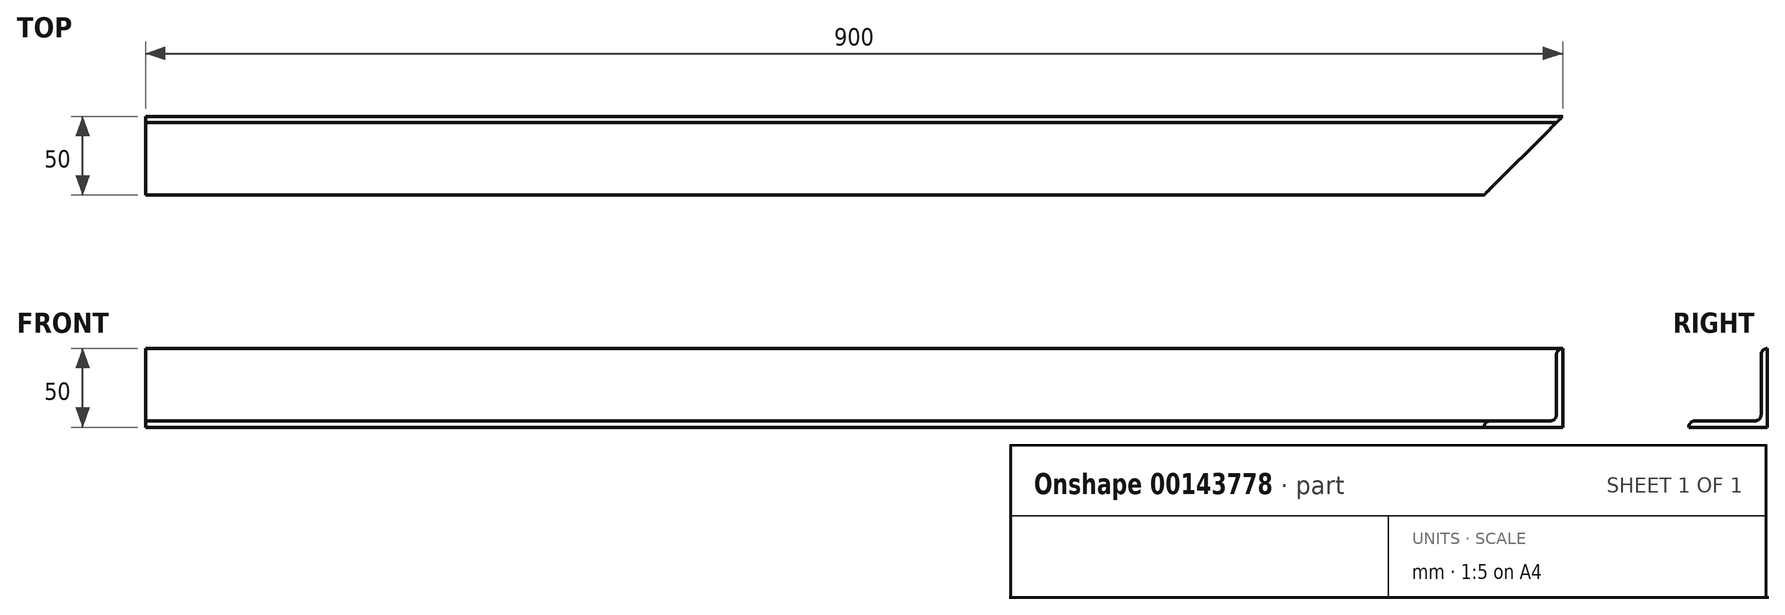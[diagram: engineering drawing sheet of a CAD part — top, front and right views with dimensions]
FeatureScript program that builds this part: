
annotation { "Feature Type Name" : "Feature", "Feature Type Description" : "" }
export const myFeature = defineFeature(function(context is Context, id is Id, definition is map)
    precondition{}
    {
        {
            var Q0;
            Q0=qCreatedBy(makeId("Right.planeOp"),FACE);
            var sketch = newSketch(context, id + "F0", { "sketchPlane" : qUnion([Q0])});
            skLineSegment(sketch, "E0", {"start": v(0, 50) * mm, "end": v(0, 0) * mm});
            skLineSegment(sketch, "E1", {"start": v(0, 0) * mm, "end": v(-50, 0) * mm});
            skLineSegment(sketch, "E2", {"start": v(0, 50) * mm, "end": v(0, 50) * mm});
            skLineSegment(sketch, "E3", {"start": v(-4, 46) * mm, "end": v(-4, 8) * mm});
            skLineSegment(sketch, "E4", {"start": v(-8, 4) * mm, "end": v(-46, 4) * mm});
            skLineSegment(sketch, "E5", {"start": v(-50, 0) * mm, "end": v(-50, 0) * mm});
            skPoint(sketch, "E6.visualSharp", {"position": v(-4, 50) * mm});
            skArc(sketch, "E6.filletArc", {"start": v(0, 50) * mm, "mid": v(-2.83, 48.83) * mm, "end": v(-4, 46) * mm});
            skPoint(sketch, "E7.visualSharp", {"position": v(-50, 4) * mm});
            skArc(sketch, "E7.filletArc", {"start": v(-46, 4) * mm, "mid": v(-48.83, 2.83) * mm, "end": v(-50, 0) * mm});
            skPoint(sketch, "E8.visualSharp", {"position": v(-4, 4) * mm});
            skArc(sketch, "E8.filletArc", {"start": v(-8, 4) * mm, "mid": v(-5.17, 5.17) * mm, "end": v(-4, 8) * mm});
            skSolve(sketch);
        }
        {
            var Q0;
            Q0=makeQuery(id+"F0.imprint","IMPRINT",FACE,{"disambiguationData":[TD([[makeQuery(id+"F0.imprint","IMPRINT",EDGE,{"derivedFrom":sQuery(id+"F0.wireOp",EDGE,"E0")}),-1.0]])]});
            extrude(context, id + "F1", {"entities" : qUnion([Q0]), "endBound" : BoundingType.SYMMETRIC, "depth" : 900 * mm});
        }
        {
            var Q0;
            Q0=makeQuery(id+"F1.opExtrude","SWEPT_FACE",FACE,{"disambiguationData":[OSD([sQuery(id+"F0.wireOp",EDGE,"E1")])]});
            var sketch = newSketch(context, id + "F2", { "sketchPlane" : qUnion([Q0])});
            skLineSegment(sketch, "E9", {"start": v(450, 0) * mm, "end": v(450, 50) * mm});
            skLineSegment(sketch, "E10", {"start": v(450, 50) * mm, "end": v(400, 50) * mm});
            skLineSegment(sketch, "E11", {"start": v(400, 50) * mm, "end": v(450, 0) * mm});
            skSolve(sketch);
        }
        {
            var Q0;
            Q0=qSketchRegion(id+"F2",true);
            extrude(context, id + "F3", {"entities" : qUnion([Q0]), "operationType" : NewBodyOperationType.REMOVE, "endBound" : BoundingType.THROUGH_ALL, "oppositeDirection" : true, "depth" : 25.4 * mm});
        }
    });
